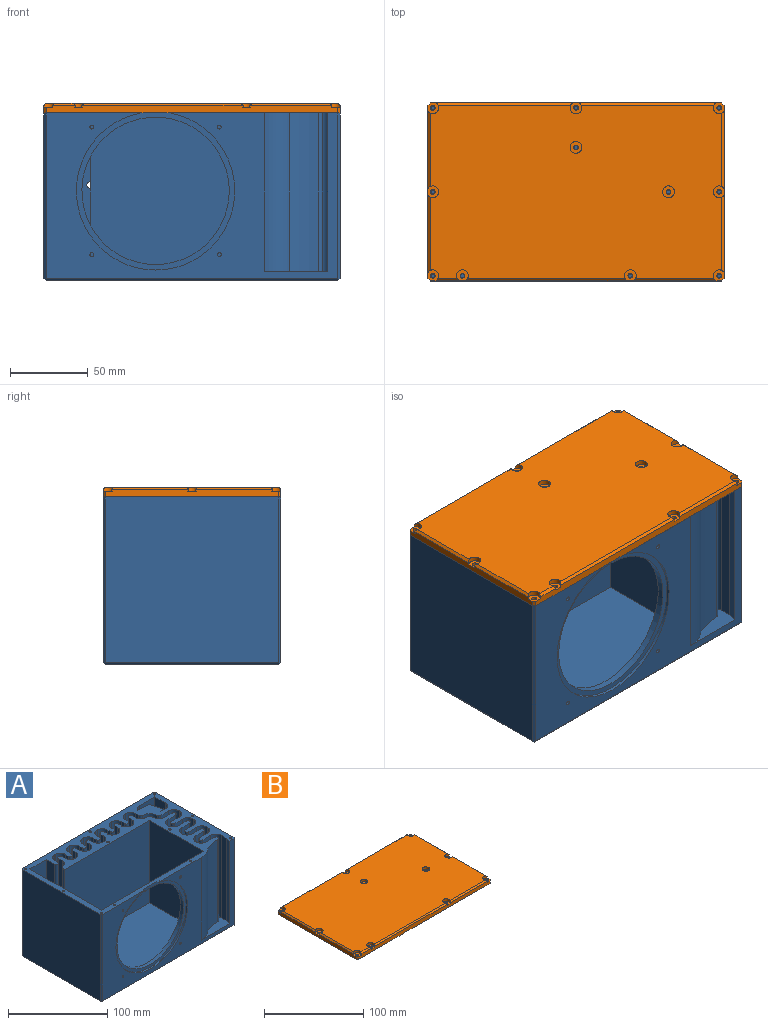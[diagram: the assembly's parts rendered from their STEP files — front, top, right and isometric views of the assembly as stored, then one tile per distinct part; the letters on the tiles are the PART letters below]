
ASSEMBLY  parts=2 mates=1
PART A: 186 faces, bbox 190.5x114.3x108 mm
  f0: cylinder r=47.38mm len=94.75mm, axis (0,-1,0), area 1294.8mm2, adj f60,f184
  f1: plane 177.8x107.95mm, normal (0,0,1), area 14188.1mm2, adj f2,f3,f8,f10,f11,f12,f16,f17
  f2: cylinder r=2.5mm len=101.6mm, axis (0,0,1), area 400.4mm2, adj f1,f12,f79,f183
  f3: plane 53.28x11.55mm, normal (-1,0,0), area 615.4mm2, adj f1,f62,f116,f158
  f4: plane 28.88x22.3mm, normal (0,0,1), area 318.8mm2, adj f13,f14,f15,f153,f154,f180,f181,f182
  f5: plane 111.3x106.45mm, normal (1,0,0), area 11847.9mm2, adj f79,f103,f104,f107
  f6: plane 187.5x106.45mm, normal (0,1,0), area 19946.8mm2, adj f79,f101,f104,f105,f116
  f7: plane 111.3x106.45mm, normal (-1,0,0), area 11847.9mm2, adj f79,f100,f105,f106
  f8: plane 187.5x106.45mm, normal (0,-1,0), area 7695.4mm2, adj f1,f27,f79,f102,f106,f107,f108,f109
  f9: plane 187.5x111.3mm, normal (0,0,-1), area 20868.8mm2, adj f100,f101,f102,f103
  f10: plane 101.6x4.19mm, normal (1,0,0), area 425.9mm2, adj f1,f79,f119,f159
  f11: plane 101.6x0.28mm, normal (0,-1,0), area 28.7mm2, adj f1,f79,f119,f152
  f12: plane 101.6x4.19mm, normal (-1,0,0), area 425.9mm2, adj f1,f2,f79,f152
  f13: plane 101.6x22.09mm, normal (0,-1,0), area 2244.1mm2, adj f4,f14,f79,f153
  f14: plane 101.6x14.94mm, normal (-1,0,0), area 1518.2mm2, adj f4,f13,f79,f154
  f15: plane 101.6x6.51mm, normal (0,1,0), area 661.2mm2, adj f4,f79,f154,f180
  f16: plane 101.6x11.34mm, normal (0,-1,0), area 1151.9mm2, adj f1,f79,f155,f177
  f17: plane 101.6x0.28mm, normal (-1,0,0), area 28.7mm2, adj f1,f79,f127,f155
  f18: plane 101.6x11.34mm, normal (0,1,0), area 1151.9mm2, adj f1,f79,f127,f163
  f19: plane 101.6x11.34mm, normal (0,-1,0), area 1151.9mm2, adj f1,f79,f126,f163
  f20: plane 101.6x0.28mm, normal (-1,0,0), area 28.7mm2, adj f1,f79,f126,f129
  f21: plane 101.6x11.34mm, normal (0,1,0), area 1151.9mm2, adj f1,f79,f129,f164
  f22: plane 101.6x11.34mm, normal (0,-1,0), area 1151.9mm2, adj f1,f79,f128,f164
  f23: plane 101.6x0.28mm, normal (-1,0,0), area 28.7mm2, adj f1,f79,f128,f131
  f24: plane 101.6x11.34mm, normal (0,1,0), area 1151.9mm2, adj f1,f79,f131,f165
  f25: plane 101.6x11.34mm, normal (0,-1,0), area 1151.9mm2, adj f1,f79,f130,f165
  f26: plane 101.6x6.94mm, normal (-1,0,0), area 705.1mm2, adj f1,f27,f79,f130
  f27: plane 101.6x6.35mm, normal (-0.97,0.24,0), area 665.4mm2, adj f1,f8,f26,f79
  f28: plane 101.6x0.04mm, normal (1,0,0), area 3.8mm2, adj f1,f79,f167,f168
  f29: plane 101.6x11.34mm, normal (0,1,0), area 1151.9mm2, adj f1,f79,f134,f168
  f30: plane 101.6x0.28mm, normal (1,0,0), area 28.7mm2, adj f1,f79,f134,f135
  f31: plane 101.6x11.34mm, normal (0,-1,0), area 1151.9mm2, adj f1,f79,f135,f169
  f32: plane 101.6x11.34mm, normal (0,1,0), area 1151.9mm2, adj f1,f79,f136,f169
  f33: plane 101.6x0.28mm, normal (1,0,0), area 28.7mm2, adj f1,f79,f136,f137
  f34: plane 101.6x11.34mm, normal (0,-1,0), area 1151.9mm2, adj f1,f79,f137,f170
  f35: plane 101.6x11.34mm, normal (0,1,0), area 1151.9mm2, adj f1,f79,f138,f170
  f36: plane 101.6x0.28mm, normal (1,0,0), area 28.7mm2, adj f1,f79,f138,f157
  f37: plane 101.6x11.34mm, normal (0,-1,0), area 1151.9mm2, adj f1,f79,f157,f178
  f38: plane 101.6x11.34mm, normal (0,1,0), area 1151.9mm2, adj f1,f79,f156,f178
  f39: plane 101.6x0.83mm, normal (1,0,0), area 84.6mm2, adj f1,f79,f156,f179
  f40: plane 101.6x0.83mm, normal (0,1,0), area 84.5mm2, adj f1,f79,f133,f179
  f41: plane 101.6x4.18mm, normal (1,0,0), area 424.6mm2, adj f1,f79,f133,f166
  f42: plane 101.6x4.18mm, normal (-1,0,0), area 424.6mm2, adj f1,f79,f132,f166
  f43: plane 101.6x0.28mm, normal (0,1,0), area 28.7mm2, adj f1,f79,f132,f141
  f44: plane 101.6x4.18mm, normal (1,0,0), area 424.6mm2, adj f1,f79,f141,f172
  f45: plane 101.6x4.18mm, normal (-1,0,0), area 424.6mm2, adj f1,f79,f142,f172
  f46: plane 101.6x0.28mm, normal (0,1,0), area 28.7mm2, adj f1,f79,f142,f143
  f47: plane 101.6x4.18mm, normal (1,0,0), area 424.6mm2, adj f1,f79,f143,f173
  f48: plane 101.6x4.18mm, normal (-1,0,0), area 424.6mm2, adj f1,f79,f144,f173
  f49: plane 101.6x0.28mm, normal (0,1,0), area 28.7mm2, adj f1,f79,f144,f145
  f50: plane 101.6x4.18mm, normal (1,0,0), area 424.6mm2, adj f1,f79,f145,f174
  f51: plane 101.6x4.18mm, normal (-1,0,0), area 424.6mm2, adj f1,f79,f146,f174
  f52: plane 101.6x0.28mm, normal (0,1,0), area 28.7mm2, adj f1,f79,f146,f147
  f53: plane 101.6x4.18mm, normal (1,0,0), area 424.6mm2, adj f1,f79,f147,f175
  f54: plane 101.6x4.18mm, normal (-1,0,0), area 424.6mm2, adj f1,f79,f148,f175
  f55: plane 101.6x0.28mm, normal (0,1,0), area 28.7mm2, adj f1,f79,f148,f151
  f56: plane 101.6x4.18mm, normal (1,0,0), area 424.6mm2, adj f1,f79,f151,f176
  f57: plane 101.6x4.93mm, normal (-1,0,0), area 501.1mm2, adj f1,f79,f150,f176
  f58: plane 121.9x101.6mm, normal (0,-1,0), area 12385mm2, adj f1,f59,f79,f115
  f59: plane 101.6x76.2mm, normal (-1,0,0), area 7741.9mm2, adj f1,f58,f60,f79
  f60: plane 145.25x101.6mm, normal (0,1,0), area 7687.3mm2, adj f0,f1,f59,f61,f79,f109,f110,f111
  f61: plane 101.6x101.6mm, normal (1,0,0), area 10322.6mm2, adj f1,f60,f62,f79
  f62: plane 101.6x23.35mm, normal (0,-1,0), area 2366.1mm2, adj f1,f3,f61,f63,f79,f116
  f63: plane 44.32x11.55mm, normal (-1,0,0), area 511.9mm2, adj f62,f79,f116,f158
  f64: plane 101.6x4.19mm, normal (1,0,0), area 425.9mm2, adj f1,f79,f149,f158
  f65: plane 101.6x0.28mm, normal (0,-1,0), area 28.7mm2, adj f1,f79,f140,f149
  f66: plane 101.6x4.19mm, normal (-1,0,0), area 425.9mm2, adj f1,f79,f140,f171
  f67: plane 101.6x4.19mm, normal (1,0,0), area 425.9mm2, adj f1,f79,f139,f171
  f68: plane 101.6x0.28mm, normal (0,-1,0), area 28.7mm2, adj f1,f79,f124,f139
  f69: plane 101.6x4.19mm, normal (-1,0,0), area 425.9mm2, adj f1,f79,f124,f162
  f70: plane 101.6x4.19mm, normal (1,0,0), area 425.9mm2, adj f1,f79,f125,f162
  f71: plane 101.6x0.28mm, normal (0,-1,0), area 28.7mm2, adj f1,f79,f122,f125
  f72: plane 101.6x4.19mm, normal (-1,0,0), area 425.9mm2, adj f1,f79,f122,f161
  f73: plane 101.6x4.19mm, normal (1,0,0), area 425.9mm2, adj f1,f79,f123,f161
  f74: plane 101.6x0.28mm, normal (0,-1,0), area 28.7mm2, adj f1,f79,f120,f123
  f75: plane 101.6x4.19mm, normal (-1,0,0), area 425.9mm2, adj f1,f79,f120,f160
  f76: plane 101.6x4.19mm, normal (1,0,0), area 425.9mm2, adj f1,f79,f121,f160
  f77: plane 101.6x0.28mm, normal (0,-1,0), area 28.7mm2, adj f1,f79,f118,f121
  f78: plane 101.6x4.19mm, normal (-1,0,0), area 425.9mm2, adj f1,f79,f118,f159
  f79: plane 190.5x114.3mm, normal (0,0,1), area 7171.3mm2, adj f2,f5,f6,f7,f8,f10,f11,f12
  f80: cylinder r=1.24mm len=7.62mm, axis (0,0,1), area 59.6mm2, adj f79,f81
  f81: plane 2.49x2.49mm, normal (0,0,1), area 4.9mm2, adj f80
  f82: cylinder r=1.24mm len=7.62mm, axis (0,0,1), area 59.6mm2, adj f79,f83
  f83: plane 2.49x2.49mm, normal (0,0,1), area 4.9mm2, adj f82
  f84: cylinder r=1.24mm len=7.62mm, axis (0,0,1), area 59.6mm2, adj f79,f85
  f85: plane 2.49x2.49mm, normal (0,0,1), area 4.9mm2, adj f84
  f86: cylinder r=1.24mm len=7.62mm, axis (0,0,1), area 59.6mm2, adj f79,f87
  f87: plane 2.49x2.49mm, normal (0,0,1), area 4.9mm2, adj f86
  f88: cylinder r=1.25mm len=7.62mm, axis (0,0,1), area 59.8mm2, adj f79,f89
  f89: plane 2.5x2.5mm, normal (0,0,1), area 4.9mm2, adj f88
  f90: cylinder r=1.24mm len=7.62mm, axis (0,0,1), area 59.6mm2, adj f79,f91
  f91: plane 2.49x2.49mm, normal (0,0,1), area 4.9mm2, adj f90
  f92: cylinder r=1.24mm len=7.62mm, axis (0,0,1), area 59.6mm2, adj f79,f93
  f93: plane 2.49x2.49mm, normal (0,0,1), area 4.9mm2, adj f92
  f94: cylinder r=1.24mm len=7.62mm, axis (0,0,1), area 59.6mm2, adj f79,f95
  f95: plane 2.49x2.49mm, normal (0,0,1), area 4.9mm2, adj f94
  f96: cylinder r=1.24mm len=7.62mm, axis (0,0,1), area 59.6mm2, adj f79,f97
  f97: plane 2.49x2.49mm, normal (0,0,1), area 4.9mm2, adj f96
  f98: cylinder r=1.24mm len=7.62mm, axis (0,0,1), area 59.6mm2, adj f79,f99
  f99: plane 2.49x2.49mm, normal (0,0,1), area 4.9mm2, adj f98
  f100: plane 112.8x1.5mm, normal (-0.71,0,-0.71), area 237.7mm2, adj f7,f9,f101,f102,f105,f106
  f101: plane 189x1.5mm, normal (0,0.71,-0.71), area 399.3mm2, adj f6,f9,f100,f103,f104,f105
  f102: plane 189x1.5mm, normal (0,-0.71,-0.71), area 399.3mm2, adj f8,f9,f100,f103,f106,f107
  f103: plane 112.8x1.5mm, normal (0.71,0,-0.71), area 237.7mm2, adj f5,f9,f101,f102,f104,f107
  f104: plane 107.2x1.5mm, normal (0.71,0.71,0), area 226.6mm2, adj f5,f6,f79,f101,f103
  f105: plane 107.2x1.5mm, normal (-0.71,0.71,0), area 226.6mm2, adj f6,f7,f79,f100,f101
  f106: plane 107.2x1.5mm, normal (-0.71,-0.71,0), area 226.6mm2, adj f7,f8,f79,f100,f102
  f107: plane 107.2x1.5mm, normal (0.71,-0.71,0), area 226.6mm2, adj f5,f8,f79,f102,f103
  f108: cylinder r=22.86mm len=101.6mm, axis (0,0,-1), area 1774mm2, adj f1,f8,f79,f117
  f109: cylinder r=1.24mm len=6.35mm, axis (0,-1,0), area 49.7mm2, adj f8,f60
  f110: cylinder r=1.24mm len=6.35mm, axis (0,-1,0), area 49.7mm2, adj f8,f60
  f111: cylinder r=1.24mm len=6.35mm, axis (0,-1,0), area 49.7mm2, adj f8,f60
  f112: cylinder r=1.24mm len=6.35mm, axis (0,-1,0), area 49.7mm2, adj f8,f60
  f113: cylinder r=1.24mm len=25.4mm, axis (0,0,1), area 198.6mm2, adj f79,f114
  f114: plane 2.49x2.49mm, normal (0,0,1), area 4.9mm2, adj f113
  f115: cylinder r=7.36mm len=101.6mm, axis (0,0,-1), area 831.4mm2, adj f1,f58,f79,f150
  f116: cylinder r=2mm len=20.33mm, axis (0,1,0), area 162.4mm2, adj f3,f6,f62,f63,f158
  f117: cylinder r=52.12mm len=101.6mm, axis (0,0,-1), area 1968.8mm2, adj f1,f79,f108,f167
  f118: cylinder r=7.36mm len=101.6mm, axis (0,0,-1), area 1174.4mm2, adj f1,f77,f78,f79
  f119: cylinder r=7.36mm len=101.6mm, axis (0,0,1), area 1174.4mm2, adj f1,f10,f11,f79
  f120: cylinder r=7.36mm len=101.6mm, axis (0,0,-1), area 1174.4mm2, adj f1,f74,f75,f79
  f121: cylinder r=7.36mm len=101.6mm, axis (0,0,1), area 1174.4mm2, adj f1,f76,f77,f79
  f122: cylinder r=7.36mm len=101.6mm, axis (0,0,-1), area 1174.4mm2, adj f1,f71,f72,f79
  f123: cylinder r=7.36mm len=101.6mm, axis (0,0,1), area 1174.4mm2, adj f1,f73,f74,f79
  f124: cylinder r=7.36mm len=101.6mm, axis (0,0,-1), area 1174.4mm2, adj f1,f68,f69,f79
  f125: cylinder r=7.36mm len=101.6mm, axis (0,0,1), area 1174.4mm2, adj f1,f70,f71,f79
  f126: cylinder r=7.36mm len=101.6mm, axis (0,0,-1), area 1174.4mm2, adj f1,f19,f20,f79
  f127: cylinder r=7.36mm len=101.6mm, axis (0,0,1), area 1174.4mm2, adj f1,f17,f18,f79
  f128: cylinder r=7.36mm len=101.6mm, axis (0,0,-1), area 1174.4mm2, adj f1,f22,f23,f79
  f129: cylinder r=7.36mm len=101.6mm, axis (0,0,1), area 1174.4mm2, adj f1,f20,f21,f79
  f130: cylinder r=7.36mm len=101.6mm, axis (0,0,-1), area 1174.4mm2, adj f1,f25,f26,f79
  f131: cylinder r=7.36mm len=101.6mm, axis (0,0,1), area 1174.4mm2, adj f1,f23,f24,f79
  f132: cylinder r=7.36mm len=101.6mm, axis (0,0,-1), area 1174.4mm2, adj f1,f42,f43,f79
  f133: cylinder r=7.36mm len=101.6mm, axis (0,0,1), area 1174.4mm2, adj f1,f40,f41,f79
  f134: cylinder r=7.36mm len=101.6mm, axis (0,0,-1), area 1174.4mm2, adj f1,f29,f30,f79
  f135: cylinder r=7.36mm len=101.6mm, axis (0,0,1), area 1174.4mm2, adj f1,f30,f31,f79
  f136: cylinder r=7.36mm len=101.6mm, axis (0,0,-1), area 1174.4mm2, adj f1,f32,f33,f79
  f137: cylinder r=7.36mm len=101.6mm, axis (0,0,1), area 1174.4mm2, adj f1,f33,f34,f79
  f138: cylinder r=7.36mm len=101.6mm, axis (0,0,-1), area 1174.4mm2, adj f1,f35,f36,f79
  f139: cylinder r=7.36mm len=101.6mm, axis (0,0,1), area 1174.4mm2, adj f1,f67,f68,f79
  f140: cylinder r=7.36mm len=101.6mm, axis (0,0,-1), area 1174.4mm2, adj f1,f65,f66,f79
  f141: cylinder r=7.36mm len=101.6mm, axis (0,0,1), area 1174.4mm2, adj f1,f43,f44,f79
  f142: cylinder r=7.36mm len=101.6mm, axis (0,0,-1), area 1174.4mm2, adj f1,f45,f46,f79
  f143: cylinder r=7.36mm len=101.6mm, axis (0,0,1), area 1174.4mm2, adj f1,f46,f47,f79
  f144: cylinder r=7.36mm len=101.6mm, axis (0,0,-1), area 1174.4mm2, adj f1,f48,f49,f79
  f145: cylinder r=7.36mm len=101.6mm, axis (0,0,1), area 1174.4mm2, adj f1,f49,f50,f79
  f146: cylinder r=7.36mm len=101.6mm, axis (0,0,-1), area 1174.4mm2, adj f1,f51,f52,f79
  f147: cylinder r=7.36mm len=101.6mm, axis (0,0,1), area 1174.4mm2, adj f1,f52,f53,f79
  f148: cylinder r=7.36mm len=101.6mm, axis (0,0,-1), area 1174.4mm2, adj f1,f54,f55,f79
  f149: cylinder r=7.36mm len=101.6mm, axis (0,0,1), area 1174.4mm2, adj f1,f64,f65,f79
  f150: cylinder r=7.36mm len=101.6mm, axis (0,0,-1), area 934.2mm2, adj f1,f57,f79,f115
  f151: cylinder r=7.36mm len=101.6mm, axis (0,0,1), area 1174.4mm2, adj f1,f55,f56,f79
  f152: cylinder r=7.36mm len=101.6mm, axis (0,0,-1), area 1174.4mm2, adj f1,f11,f12,f79
  f153: cylinder r=7.36mm len=101.6mm, axis (0,0,1), area 878.4mm2, adj f4,f13,f79,f182
  f154: cylinder r=7.36mm len=101.6mm, axis (0,0,1), area 1174.4mm2, adj f4,f14,f15,f79
  f155: cylinder r=7.36mm len=101.6mm, axis (0,0,-1), area 1174.4mm2, adj f1,f16,f17,f79
  f156: cylinder r=7.36mm len=101.6mm, axis (0,0,-1), area 1174.4mm2, adj f1,f38,f39,f79
  f157: cylinder r=7.36mm len=101.6mm, axis (0,0,1), area 1174.4mm2, adj f1,f36,f37,f79
  f158: cylinder r=2.5mm len=101.6mm, axis (0,0,1), area 786.6mm2, adj f1,f3,f63,f64,f79,f116
  f159: cylinder r=2.5mm len=101.6mm, axis (0,0,1), area 798mm2, adj f1,f10,f78,f79
  f160: cylinder r=2.5mm len=101.6mm, axis (0,0,1), area 798mm2, adj f1,f75,f76,f79
  f161: cylinder r=2.5mm len=101.6mm, axis (0,0,1), area 798mm2, adj f1,f72,f73,f79
  f162: cylinder r=2.5mm len=101.6mm, axis (0,0,1), area 798mm2, adj f1,f69,f70,f79
  f163: cylinder r=2.5mm len=101.6mm, axis (0,0,1), area 798mm2, adj f1,f18,f19,f79
  f164: cylinder r=2.5mm len=101.6mm, axis (0,0,1), area 798mm2, adj f1,f21,f22,f79
  f165: cylinder r=2.5mm len=101.6mm, axis (0,0,1), area 798mm2, adj f1,f24,f25,f79
  f166: cylinder r=2.5mm len=101.6mm, axis (0,0,-1), area 798mm2, adj f1,f41,f42,f79
  f167: cylinder r=2.5mm len=101.6mm, axis (0,0,-1), area 389.5mm2, adj f1,f28,f79,f117
  f168: cylinder r=2.5mm len=101.6mm, axis (0,0,-1), area 399mm2, adj f1,f28,f29,f79
  f169: cylinder r=2.5mm len=101.6mm, axis (0,0,-1), area 798mm2, adj f1,f31,f32,f79
  f170: cylinder r=2.5mm len=101.6mm, axis (0,0,-1), area 798mm2, adj f1,f34,f35,f79
  f171: cylinder r=2.5mm len=101.6mm, axis (0,0,1), area 798mm2, adj f1,f66,f67,f79
  f172: cylinder r=2.5mm len=101.6mm, axis (0,0,-1), area 798mm2, adj f1,f44,f45,f79
  f173: cylinder r=2.5mm len=101.6mm, axis (0,0,-1), area 798mm2, adj f1,f47,f48,f79
  f174: cylinder r=2.5mm len=101.6mm, axis (0,0,-1), area 798mm2, adj f1,f50,f51,f79
  f175: cylinder r=2.5mm len=101.6mm, axis (0,0,-1), area 798mm2, adj f1,f53,f54,f79
  f176: cylinder r=2.5mm len=101.6mm, axis (0,0,-1), area 798mm2, adj f1,f56,f57,f79
  f177: cylinder r=2.5mm len=101.6mm, axis (0,0,1), area 400.4mm2, adj f1,f16,f79,f183
  f178: cylinder r=2.5mm len=101.6mm, axis (0,0,-1), area 798mm2, adj f1,f37,f38,f79
  f179: cylinder r=5.06mm len=101.6mm, axis (0,0,-1), area 807.5mm2, adj f1,f39,f40,f79
  f180: plane 101.6x4.99mm, normal (0.32,-0.95,0), area 536.1mm2, adj f4,f15,f79,f181
  f181: plane 101.6x14.66mm, normal (0.96,0.26,0), area 1543.5mm2, adj f4,f79,f180,f182
  f182: plane 101.6x16mm, normal (0.09,1,0), area 1632.3mm2, adj f4,f79,f153,f181
  f183: cylinder r=10.71mm len=101.6mm, axis (0,0,1), area 1714.5mm2, adj f1,f2,f79,f177
  f184: plane 101.87x100.99mm, normal (0,-1,0), area 1088.3mm2, adj f0,f79,f185
  f185: cylinder r=50.94mm len=101.87mm, axis (0,-1,0), area 602mm2, adj f8,f79,f184
PART B: 54 faces, bbox 190.5x114.3x6.4 mm
  f0: cylinder r=1.5mm len=3.35mm, axis (0,0,-1), area 31.6mm2, adj f25,f33
  f1: cylinder r=1.5mm len=3.35mm, axis (0,0,-1), area 31.6mm2, adj f25,f31
  f2: cylinder r=1.5mm len=3.35mm, axis (0,0,-1), area 31.6mm2, adj f25,f37
  f3: cylinder r=1.5mm len=3.35mm, axis (0,0,-1), area 31.6mm2, adj f25,f35
  f4: cylinder r=1.5mm len=3.35mm, axis (0,0,-1), area 31.5mm2, adj f25,f46
  f5: cylinder r=1.5mm len=3.35mm, axis (0,0,-1), area 31.6mm2, adj f25,f41
  f6: cylinder r=1.5mm len=3.35mm, axis (0,0,-1), area 31.6mm2, adj f25,f43
  f7: cylinder r=1.5mm len=3.35mm, axis (0,0,-1), area 31.6mm2, adj f25,f44
  f8: cylinder r=1.5mm len=3.35mm, axis (0,0,-1), area 31.6mm2, adj f25,f51
  f9: cylinder r=1.5mm len=3.35mm, axis (0,0,-1), area 31.6mm2, adj f25,f49
  f10: cylinder r=1.5mm len=3.35mm, axis (0,0,-1), area 31.5mm2, adj f25,f39
  f11: plane 87.86x1.5mm, normal (0,0.71,0.71), area 183.1mm2, adj f22,f24,f34,f47
  f12: plane 49.76x1.5mm, normal (0.71,0,0.71), area 102.3mm2, adj f21,f24,f36,f45
  f13: plane 49.76x1.5mm, normal (-0.71,0,0.71), area 102.3mm2, adj f23,f24,f32,f42
  f14: plane 103.74x1.5mm, normal (0,-0.71,0.71), area 216.8mm2, adj f20,f24,f38,f40
  f15: plane 14.84x1.5mm, normal (0,-0.71,0.71), area 28.2mm2, adj f20,f24,f30,f38
  f16: plane 3.35x1.5mm, normal (0.71,-0.71,0), area 7.1mm2, adj f20,f21,f25,f37
  f17: plane 3.35x1.5mm, normal (0.71,0.71,0), area 7.1mm2, adj f21,f22,f25,f35
  f18: plane 3.35x1.5mm, normal (-0.71,0.71,0), area 7.1mm2, adj f22,f23,f25,f33
  f19: plane 3.35x1.5mm, normal (-0.71,-0.71,0), area 7.1mm2, adj f20,f23,f25,f31
  f20: plane 187.5x4.85mm, normal (0,-1,0), area 879.4mm2, adj f14,f15,f16,f19,f25,f29,f30,f31
  f21: plane 111.3x4.85mm, normal (1,0,0), area 522.1mm2, adj f12,f16,f17,f25,f27,f34,f35,f36
  f22: plane 187.5x4.85mm, normal (0,1,0), area 891.7mm2, adj f11,f17,f18,f25,f26,f32,f33,f34
  f23: plane 111.3x4.85mm, normal (-1,0,0), area 522.1mm2, adj f13,f18,f19,f25,f28,f30,f31,f32
  f24: plane 187.5x111.3mm, normal (0,0,1), area 20495.7mm2, adj f11,f12,f13,f14,f15,f26,f27,f28
  f25: plane 190.5x114.3mm, normal (0,0,-1), area 21654.1mm2, adj f0,f1,f2,f3,f4,f5,f6,f7
  f26: plane 87.86x1.5mm, normal (0,0.71,0.71), area 183.1mm2, adj f22,f24,f32,f47
  f27: plane 49.76x1.5mm, normal (0.71,0,0.71), area 102.3mm2, adj f21,f24,f34,f45
  f28: plane 49.76x1.5mm, normal (-0.71,0,0.71), area 102.3mm2, adj f23,f24,f30,f42
  f29: plane 52.94x1.5mm, normal (0,-0.71,0.71), area 109mm2, adj f20,f24,f36,f40
  f30: cylinder r=3.81mm len=6.99mm, axis (0,0,1), area 37.2mm2, adj f15,f20,f23,f24,f28,f31
  f31: plane 6.99x6.99mm, normal (0,0,1), area 34.3mm2, adj f1,f19,f20,f23,f30
  f32: cylinder r=3.81mm len=6.99mm, axis (0,0,1), area 37.2mm2, adj f13,f22,f23,f24,f26,f33
  f33: plane 6.99x6.99mm, normal (0,0,1), area 34.3mm2, adj f0,f18,f22,f23,f32
  f34: cylinder r=3.81mm len=6.99mm, axis (0,0,1), area 37.2mm2, adj f11,f21,f22,f24,f27,f35
  f35: plane 6.99x6.99mm, normal (0,0,1), area 34.3mm2, adj f3,f17,f21,f22,f34
  f36: cylinder r=3.81mm len=6.99mm, axis (0,0,1), area 37.2mm2, adj f12,f20,f21,f24,f29,f37
  f37: plane 6.99x6.99mm, normal (0,0,1), area 34.3mm2, adj f2,f16,f20,f21,f36
  f38: cylinder r=3.81mm len=7.62mm, axis (0,0,1), area 55.2mm2, adj f14,f15,f20,f24,f39
  f39: plane 7.62x6.99mm, normal (0,0,1), area 36.7mm2, adj f10,f20,f38
  f40: cylinder r=3.81mm len=7.62mm, axis (0,0,1), area 55.2mm2, adj f14,f20,f24,f29,f41
  f41: plane 7.62x6.99mm, normal (0,0,1), area 36.7mm2, adj f5,f20,f40
  f42: cylinder r=3.81mm len=7.62mm, axis (0,0,1), area 55.2mm2, adj f13,f23,f24,f28,f43
  f43: plane 7.62x6.99mm, normal (0,0,1), area 36.7mm2, adj f6,f23,f42
  f44: plane 7.62x6.99mm, normal (0,0,1), area 36.7mm2, adj f7,f21,f45
  f45: cylinder r=3.81mm len=7.62mm, axis (0,0,1), area 55.2mm2, adj f12,f21,f24,f27,f44
  f46: plane 7.62x6.99mm, normal (0,0,1), area 36.7mm2, adj f4,f22,f47
  f47: cylinder r=3.81mm len=7.62mm, axis (0,0,1), area 55.2mm2, adj f11,f22,f24,f26,f46
  f48: cylinder r=3.81mm len=7.62mm, axis (0,0,1), area 71.8mm2, adj f24,f49
  f49: plane 7.62x7.62mm, normal (0,0,1), area 38.5mm2, adj f9,f48
  f50: cylinder r=3.81mm len=7.62mm, axis (0,0,1), area 71.8mm2, adj f24,f51
  f51: plane 7.62x7.62mm, normal (0,0,1), area 38.5mm2, adj f8,f50
  f52: cylinder r=94.74mm len=18.9mm, axis (0,-1,0), area 37.9mm2, adj f20,f25,f53
  f53: plane 18.9x0.47mm, normal (0,-1,0), area 6mm2, adj f25,f52
PLACE A at identity
PLACE B t=(0,0,107.95)mm
MATE revolute B.f1 <-> A.f86  axis (0,0,-1) through (-92.08,-53.98,107.95)mm
